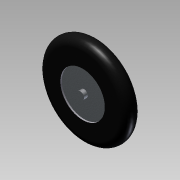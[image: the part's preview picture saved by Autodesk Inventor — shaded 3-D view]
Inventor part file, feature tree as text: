
AUTODESK INVENTOR PART (.ipt)
format: ipt  version: 2012 (Build 160160000, 160)  size: 127,488 bytes
history: native  units: in
note: dims shown in document units (in); Inventor stores cm internally (conversion verified against a paired STEP export)
features: extrude x5, sketch x5, fillet x1
ambient origin geometry x8: Origin, YZ Plane, XZ Plane, XY Plane, X Axis, Y Axis, Z Axis, Center Point
bodies: Solid1 (feature_tree)
feature tree (11):
  extrude  "Extrusion1"  Depth=1.0in TaperAngle=0.0deg
  extrude  "Extrusion2"  Depth=0.1in TaperAngle=0.0deg
  extrude  "Extrusion3"  Depth=0.1in TaperAngle=0.0deg
  fillet  "Fillet1"  Radius=0.5in
  extrude  "Extrusion4"  Depth=0.25in TaperAngle=0.0deg
  extrude  "Extrusion5"  Depth=0.25in TaperAngle=0.0deg
  sketch  "Sketch1"  dims[d0=6.0in d1=1.0in d2=0.0in]
  sketch  "Sketch2"  dims[d3=3.0in d4=0.1in d5=0.0in]
  sketch  "Sketch3"  dims[d6=3.0in d7=0.1in d8=0.0in d9=0.5in]
  sketch  "Sketch4"  dims[d10=0.5in d11=0.25in d12=0.0in]
  sketch  "Sketch5"  dims[d13=0.5in d14=0.25in d15=0.0in]
